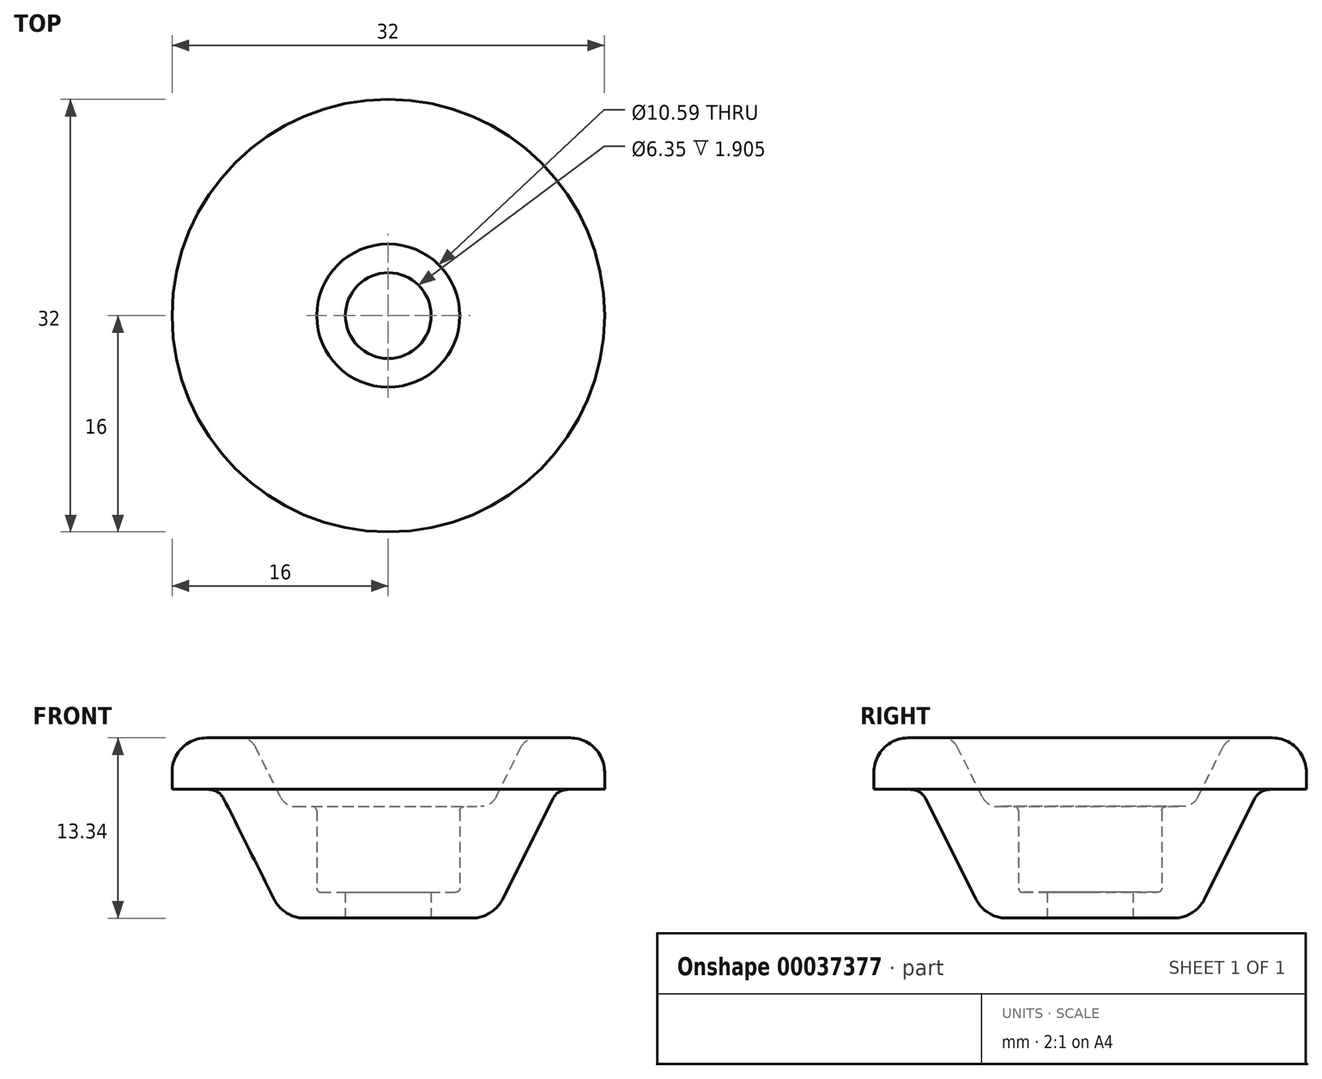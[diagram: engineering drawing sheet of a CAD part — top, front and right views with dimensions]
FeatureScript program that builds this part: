
annotation { "Feature Type Name" : "Feature", "Feature Type Description" : "" }
export const myFeature = defineFeature(function(context is Context, id is Id, definition is map)
    precondition{}
    {
        {
            var Q0;
            Q0=qCreatedBy(makeId("Front.planeOp"),FACE);
            var sketch = newSketch(context, id + "F0", { "sketchPlane" : qUnion([Q0])});
            skLineSegment(sketch, "E0", {"start": v(5.61, 0) * mm, "end": v(6.84, 0) * mm});
            skLineSegment(sketch, "E1", {"start": v(7.97, 0.7) * mm, "end": v(9.8, 4.38) * mm});
            skLineSegment(sketch, "E2", {"start": v(10.94, 5.08) * mm, "end": v(13.46, 5.08) * mm});
            skLineSegment(sketch, "E3.0", {"start": v(8.45, -6.85) * mm, "end": v(12.16, 0.57) * mm});
            skLineSegment(sketch, "E4.0", {"start": v(13.3, 1.27) * mm, "end": v(16, 1.27) * mm});
            skLineSegment(sketch, "E5", {"start": v(3.18, -8.26) * mm, "end": v(6.18, -8.26) * mm});
            skLineSegment(sketch, "E6", {"start": v(5.3, -0.32) * mm, "end": v(5.3, -6.03) * mm});
            skLineSegment(sketch, "E7", {"start": v(4.98, -6.35) * mm, "end": v(3.18, -6.35) * mm});
            skLineSegment(sketch, "E8", {"start": v(3.17, -6.35) * mm, "end": v(3.17, -8.26) * mm});
            skLineSegment(sketch, "E9", {"start": v(16, 2.54) * mm, "end": v(16, 1.27) * mm});
            skPoint(sketch, "E10.visualSharp", {"position": v(10.16, 5.08) * mm});
            skArc(sketch, "E10.filletArc", {"start": v(10.94, 5.08) * mm, "mid": v(10.28, 4.9) * mm, "end": v(9.8, 4.38) * mm});
            skPoint(sketch, "E11.visualSharp", {"position": v(16, 5.08) * mm});
            skArc(sketch, "E11.filletArc", {"start": v(16, 2.54) * mm, "mid": v(15.26, 4.34) * mm, "end": v(13.46, 5.08) * mm});
            skPoint(sketch, "E12.visualSharp", {"position": v(12.51, 1.27) * mm});
            skArc(sketch, "E12.filletArc", {"start": v(13.3, 1.27) * mm, "mid": v(12.63, 1.08) * mm, "end": v(12.16, 0.57) * mm});
            skPoint(sketch, "E13.visualSharp", {"position": v(7.75, -8.26) * mm});
            skArc(sketch, "E13.filletArc", {"start": v(6.18, -8.26) * mm, "mid": v(7.52, -7.88) * mm, "end": v(8.45, -6.85) * mm});
            skPoint(sketch, "E14.visualSharp", {"position": v(5.3, -6.35) * mm});
            skArc(sketch, "E14.filletArc", {"start": v(4.98, -6.35) * mm, "mid": v(5.2, -6.26) * mm, "end": v(5.3, -6.03) * mm});
            skPoint(sketch, "E15.visualSharp", {"position": v(5.3, 0) * mm});
            skArc(sketch, "E15.filletArc", {"start": v(5.61, 0) * mm, "mid": v(5.39, -0.1) * mm, "end": v(5.3, -0.32) * mm});
            skPoint(sketch, "E16.visualSharp", {"position": v(7.62, 0) * mm});
            skArc(sketch, "E16.filletArc", {"start": v(6.84, 0) * mm, "mid": v(7.5, 0.19) * mm, "end": v(7.97, 0.7) * mm});
            skLineSegment(sketch, "E17", {"start": v(0, 0) * mm, "end": v(0, 11.05) * mm});
            skSolve(sketch);
        }
        {
            var Q0;
            Q0=makeQuery(id+"F0.imprint","IMPRINT",FACE,{"disambiguationData":[TD([[makeQuery(id+"F0.imprint","IMPRINT",EDGE,{"derivedFrom":sQuery(id+"F0.wireOp",EDGE,"E0")}),-1.0]])]});
            var Q1;
            Q1=sQuery(id+"F0.wireOp",EDGE,"E17");
            revolve(context, id + "F1", {"entities" : qUnion([Q0]), "axis" : qUnion([Q1]), "revolveType" : RevolveType.FULL});
        }
    });
